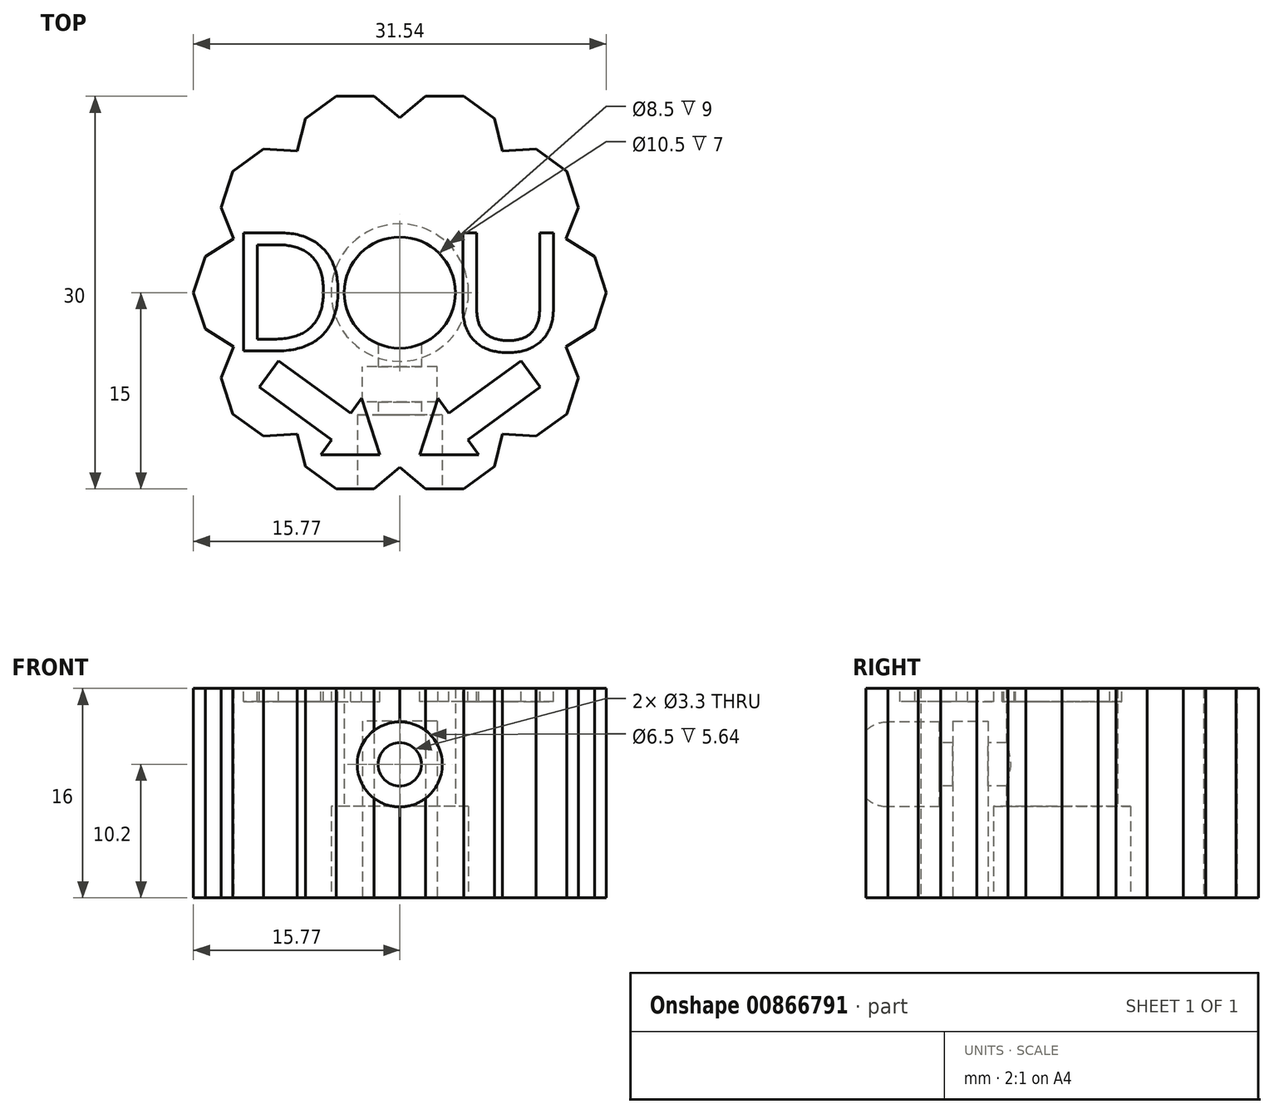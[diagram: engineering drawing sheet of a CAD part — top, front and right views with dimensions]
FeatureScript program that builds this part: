
annotation { "Feature Type Name" : "Feature", "Feature Type Description" : "" }
export const myFeature = defineFeature(function(context is Context, id is Id, definition is map)
    precondition{}
    {
        {
            var Q0;
            Q0=qCreatedBy(makeId("Top.planeOp"),FACE);
            var sketch = newSketch(context, id + "F0", { "sketchPlane" : qUnion([Q0])});
            skCircle(sketch, "E0", {"center": v(0, 0) * mm, "radius": 4.25 * mm});
            skCircle(sketch, "E1.cCircle", {"center": v(0, 0) * mm, "radius": 15 * mm, "construction": true});
            skLineSegment(sketch, "E1.0", {"start": v(15.77, 0) * mm, "end": v(12.76, -9.27) * mm});
            skLineSegment(sketch, "E1.1", {"start": v(12.76, -9.27) * mm, "end": v(4.87, -15) * mm});
            skLineSegment(sketch, "E1.2", {"start": v(4.87, -15) * mm, "end": v(-4.87, -15) * mm});
            skLineSegment(sketch, "E1.3", {"start": v(-4.87, -15) * mm, "end": v(-12.76, -9.27) * mm});
            skLineSegment(sketch, "E1.4", {"start": v(-12.76, -9.27) * mm, "end": v(-15.77, 0) * mm});
            skLineSegment(sketch, "E1.5", {"start": v(-15.77, 0) * mm, "end": v(-12.76, 9.27) * mm});
            skLineSegment(sketch, "E1.6", {"start": v(-12.76, 9.27) * mm, "end": v(-4.87, 15) * mm});
            skLineSegment(sketch, "E1.7", {"start": v(-4.87, 15) * mm, "end": v(4.87, 15) * mm});
            skLineSegment(sketch, "E1.8", {"start": v(4.87, 15) * mm, "end": v(12.76, 9.27) * mm});
            skLineSegment(sketch, "E1.9", {"start": v(12.76, 9.27) * mm, "end": v(15.77, 0) * mm});
            skPoint(sketch, "E1.0.midPoint", {"position": v(14.27, -4.64) * mm});
            skCircle(sketch, "E2", {"center": v(0, 0) * mm, "radius": 5.25 * mm});
            skLineSegment(sketch, "E3.bottom", {"start": v(2.85, -8.35) * mm, "end": v(-2.85, -8.35) * mm});
            skLineSegment(sketch, "E3.top", {"start": v(2.85, -5.65) * mm, "end": v(-2.85, -5.65) * mm});
            skLineSegment(sketch, "E3.left", {"start": v(2.85, -8.35) * mm, "end": v(2.85, -5.65) * mm});
            skLineSegment(sketch, "E3.right", {"start": v(-2.85, -8.35) * mm, "end": v(-2.85, -5.65) * mm});
            skPoint(sketch, "E3.middle", {"position": v(0, -7) * mm});
            skLineSegment(sketch, "E4", {"start": v(-1.97, -15) * mm, "end": v(0, -13.36) * mm});
            skPoint(sketch, "E4.endSnap0", {"position": v(0, -15) * mm});
            skLineSegment(sketch, "E5.MirrorCS", {"start": v(1.97, -15) * mm, "end": v(0, -13.36) * mm});
            skLineSegment(sketch, "E6.1.0", {"start": v(10.41, -10.98) * mm, "end": v(7.85, -10.8) * mm});
            skLineSegment(sketch, "E6.1.1", {"start": v(7.22, -13.3) * mm, "end": v(7.85, -10.8) * mm});
            skLineSegment(sketch, "E6.2.0", {"start": v(14.88, -2.76) * mm, "end": v(12.7, -4.13) * mm});
            skLineSegment(sketch, "E6.2.1", {"start": v(13.66, -6.51) * mm, "end": v(12.7, -4.13) * mm});
            skLineSegment(sketch, "E6.3.0", {"start": v(13.66, 6.51) * mm, "end": v(12.7, 4.13) * mm});
            skLineSegment(sketch, "E6.3.1", {"start": v(14.88, 2.76) * mm, "end": v(12.7, 4.13) * mm});
            skLineSegment(sketch, "E6.4.0", {"start": v(7.22, 13.3) * mm, "end": v(7.85, 10.8) * mm});
            skLineSegment(sketch, "E6.4.1", {"start": v(10.41, 10.98) * mm, "end": v(7.85, 10.8) * mm});
            skLineSegment(sketch, "E6.5.0", {"start": v(-1.97, 15) * mm, "end": v(0, 13.36) * mm});
            skLineSegment(sketch, "E6.5.1", {"start": v(1.97, 15) * mm, "end": v(0, 13.36) * mm});
            skLineSegment(sketch, "E6.6.0", {"start": v(-10.41, 10.98) * mm, "end": v(-7.85, 10.8) * mm});
            skLineSegment(sketch, "E6.6.1", {"start": v(-7.22, 13.3) * mm, "end": v(-7.85, 10.8) * mm});
            skLineSegment(sketch, "E6.7.0", {"start": v(-14.88, 2.76) * mm, "end": v(-12.7, 4.13) * mm});
            skLineSegment(sketch, "E6.7.1", {"start": v(-13.66, 6.51) * mm, "end": v(-12.7, 4.13) * mm});
            skLineSegment(sketch, "E6.8.0", {"start": v(-13.66, -6.51) * mm, "end": v(-12.7, -4.13) * mm});
            skLineSegment(sketch, "E6.8.1", {"start": v(-14.88, -2.76) * mm, "end": v(-12.7, -4.13) * mm});
            skLineSegment(sketch, "E6.9.0", {"start": v(-7.22, -13.3) * mm, "end": v(-7.85, -10.8) * mm});
            skLineSegment(sketch, "E6.9.1", {"start": v(-10.41, -10.98) * mm, "end": v(-7.85, -10.8) * mm});
            skSolve(sketch);
        }
        {
            var Q0;
            Q0=makeQuery(id+"F0.imprint","IMPRINT",FACE,{"disambiguationData":[TD([[makeQuery(id+"F0.imprint","IMPRINT",EDGE,{"derivedFrom":sQuery(id+"F0.wireOp",EDGE,"E0")}),-1.0]])]});
            var Q1;
            Q1=makeQuery(id+"F0.imprint","IMPRINT",FACE,{"disambiguationData":[TD([[makeQuery(id+"F0.imprint","IMPRINT",EDGE,{"derivedFrom":sQuery(id+"F0.wireOp",EDGE,"E1.0")}),-1.0]])]});
            var Q2;
            Q2=makeQuery(id+"F0.imprint","IMPRINT",FACE,{"disambiguationData":[TD([[makeQuery(id+"F0.imprint","IMPRINT",EDGE,{"derivedFrom":sQuery(id+"F0.wireOp",EDGE,"E3.bottom")}),-1.0]])]});
            extrude(context, id + "F1", {"entities" : qUnion([Q0, Q1, Q2]), "depth" : 16 * mm, "offsetDistance" : 25 * mm});
        }
        {
            var Q0;
            Q0=makeQuery(id+"F0.imprint","IMPRINT",FACE,{"disambiguationData":[TD([[makeQuery(id+"F0.imprint","IMPRINT",EDGE,{"derivedFrom":sQuery(id+"F0.wireOp",EDGE,"E0")}),-1.0]])]});
            extrude(context, id + "F2", {"entities" : qUnion([Q0]), "operationType" : NewBodyOperationType.REMOVE, "depth" : 7 * mm, "offsetDistance" : 25 * mm});
        }
        {
            var Q0;
            Q0=makeQuery(id+"F0.imprint","IMPRINT",FACE,{"disambiguationData":[TD([[makeQuery(id+"F0.imprint","IMPRINT",EDGE,{"derivedFrom":sQuery(id+"F0.wireOp",EDGE,"E3.bottom")}),-1.0]])]});
            extrude(context, id + "F3", {"entities" : qUnion([Q0]), "operationType" : NewBodyOperationType.REMOVE, "depth" : 13.5 * mm, "offsetDistance" : 25 * mm});
        }
        {
            var Q0;
            Q0=makeQuery(id+"F1.opExtrude","SWEPT_FACE",FACE,{"disambiguationData":[OSD([sQuery(id+"F0.wireOp",EDGE,"E1.2")])]});
            var sketch = newSketch(context, id + "F4", { "sketchPlane" : qUnion([Q0])});
            skPoint(sketch, "E7", {"position": v(0, 10.2) * mm});
            skSolve(sketch);
        }
        {
            var Q0;
            Q0=sQuery(id+"F4.wireOp",VERTEX,"E7");
            var Q1;
            Q1=makeQuery(id+"F1.opExtrude","SWEPT_BODY",BODY,{"disambiguationData":[OSD([sQuery(id+"F0.wireOp",EDGE,"E0"),sQuery(id+"F0.wireOp",EDGE,"E1.0"),sQuery(id+"F0.wireOp",EDGE,"E1.1"),sQuery(id+"F0.wireOp",EDGE,"E1.2"),sQuery(id+"F0.wireOp",EDGE,"E1.3"),sQuery(id+"F0.wireOp",EDGE,"E1.4"),sQuery(id+"F0.wireOp",EDGE,"E1.5"),sQuery(id+"F0.wireOp",EDGE,"E1.6"),sQuery(id+"F0.wireOp",EDGE,"E1.7"),sQuery(id+"F0.wireOp",EDGE,"E1.8"),sQuery(id+"F0.wireOp",EDGE,"E1.9")])]});
            hole(context, id + "F5", {"style" : HoleStyle.C_BORE, "endStyle" : HoleEndStyle.BLIND, "holeDiameter" : 3.3 * mm, "cBoreDiameter" : 6.5 * mm, "cBoreDepth" : 4 * mm, "majorDiameter" : 5 * mm, "holeDepth" : 12 * mm, "isTappedThrough" : true, "tappedDepth" : 12 * mm, "tapClearance" : 3, "locations" : qUnion([Q0]), "scope" : qUnion([Q1])});
        }
        {
            var Q0;
            Q0=makeQuery(id+"F1.opExtrude","CAP_FACE",FACE,{"disambiguationData":[OSD([sQuery(id+"F0.wireOp",EDGE,"E0"),sQuery(id+"F0.wireOp",EDGE,"E1.0"),sQuery(id+"F0.wireOp",EDGE,"E1.1"),sQuery(id+"F0.wireOp",EDGE,"E1.2"),sQuery(id+"F0.wireOp",EDGE,"E1.3"),sQuery(id+"F0.wireOp",EDGE,"E1.4"),sQuery(id+"F0.wireOp",EDGE,"E1.5"),sQuery(id+"F0.wireOp",EDGE,"E1.6"),sQuery(id+"F0.wireOp",EDGE,"E1.7"),sQuery(id+"F0.wireOp",EDGE,"E1.8"),sQuery(id+"F0.wireOp",EDGE,"E1.9")])],"isStart":false});
            var sketch = newSketch(context, id + "F6", { "sketchPlane" : qUnion([Q0])});
            skText(sketch, "E8", { "text": "D", "fontName": "OpenSans-Regular.ttf"});
            skText(sketch, "E9", { "text": "U\n", "fontName": "OpenSans-Regular.ttf"});
            skLineSegment(sketch, "E10", {"start": v(-10.74, -7.22) * mm, "end": v(-5.21, -11.24) * mm});
            skLineSegment(sketch, "E11", {"start": v(-5.21, -11.24) * mm, "end": v(-6.04, -12.38) * mm});
            skLineSegment(sketch, "E12", {"start": v(-6.04, -12.38) * mm, "end": v(-1.52, -12.38) * mm});
            skLineSegment(sketch, "E13", {"start": v(-1.52, -12.38) * mm, "end": v(-10, -6.21) * mm});
            skLineSegment(sketch, "E14", {"start": v(-10, -6.21) * mm, "end": v(-10.74, -7.22) * mm});
            skLineSegment(sketch, "E15.MirrorCS", {"start": v(-10, -6.21) * mm, "end": v(-9.28, -5.2) * mm});
            skLineSegment(sketch, "E16.MirrorCS", {"start": v(-9.28, -5.2) * mm, "end": v(-3.75, -9.22) * mm});
            skLineSegment(sketch, "E17.MirrorCS", {"start": v(-3.75, -9.22) * mm, "end": v(-2.92, -8.08) * mm});
            skLineSegment(sketch, "E18.MirrorCS", {"start": v(-2.92, -8.08) * mm, "end": v(-1.52, -12.38) * mm});
            skLineSegment(sketch, "E19.MirrorCS", {"start": v(9.28, -5.2) * mm, "end": v(3.75, -9.22) * mm});
            skLineSegment(sketch, "E20.MirrorCS", {"start": v(10, -6.21) * mm, "end": v(9.28, -5.2) * mm});
            skLineSegment(sketch, "E21.MirrorCS", {"start": v(10, -6.21) * mm, "end": v(10.74, -7.22) * mm});
            skLineSegment(sketch, "E22.MirrorCS", {"start": v(10.74, -7.22) * mm, "end": v(5.21, -11.24) * mm});
            skLineSegment(sketch, "E23.MirrorCS", {"start": v(5.21, -11.24) * mm, "end": v(6.04, -12.38) * mm});
            skLineSegment(sketch, "E24.MirrorCS", {"start": v(6.04, -12.38) * mm, "end": v(1.52, -12.38) * mm});
            skLineSegment(sketch, "E25.MirrorCS", {"start": v(2.92, -8.08) * mm, "end": v(1.52, -12.38) * mm});
            skLineSegment(sketch, "E26.MirrorCS", {"start": v(3.75, -9.22) * mm, "end": v(2.92, -8.08) * mm});
            const initialGuessF6  = {"E8": [-0.01317, -0.00446, 1, 0, 0.0091], "E9": [0.00368, -0.00446, 1, 0, 0.0091]};
            skSetInitialGuess(sketch, initialGuessF6);
            skSolve(sketch);
        }
        {
            var Q0;
            Q0=makeQuery(id+"F6.imprint","IMPRINT",FACE,{"disambiguationData":[TD([[makeQuery(id+"F6.imprint","IMPRINT",EDGE,{"derivedFrom":sQuery(id+"F6.wireOp",EDGE,"E8.sketch_text.stroke-0")}),-1.0]])]});
            var Q1;
            Q1=makeQuery(id+"F6.imprint","IMPRINT",FACE,{"disambiguationData":[TD([[makeQuery(id+"F6.imprint","IMPRINT",EDGE,{"derivedFrom":sQuery(id+"F6.wireOp",EDGE,"E9.sketch_text.stroke-0")}),-1.0]])]});
            var Q2;
            Q2=makeQuery(id+"F6.imprint","IMPRINT",FACE,{"disambiguationData":[TD([[makeQuery(id+"F6.imprint","IMPRINT",EDGE,{"derivedFrom":sQuery(id+"F6.wireOp",EDGE,"E10")}),1.0]])]});
            var Q3;
            Q3=makeQuery(id+"F6.imprint","IMPRINT",FACE,{"disambiguationData":[TD([[makeQuery(id+"F6.imprint","IMPRINT",EDGE,{"derivedFrom":sQuery(id+"F6.wireOp",EDGE,"E13")}),-1.0]])]});
            var Q4;
            Q4=makeQuery(id+"F6.imprint","IMPRINT",FACE,{"disambiguationData":[TD([[makeQuery(id+"F6.imprint","IMPRINT",EDGE,{"derivedFrom":sQuery(id+"F6.wireOp",EDGE,"E19.MirrorCS")}),1.0]])]});
            extrude(context, id + "F7", {"entities" : qUnion([Q0, Q1, Q2, Q3, Q4]), "operationType" : NewBodyOperationType.REMOVE, "oppositeDirection" : true, "depth" : 1 * mm, "offsetDistance" : 25 * mm});
        }
    });
